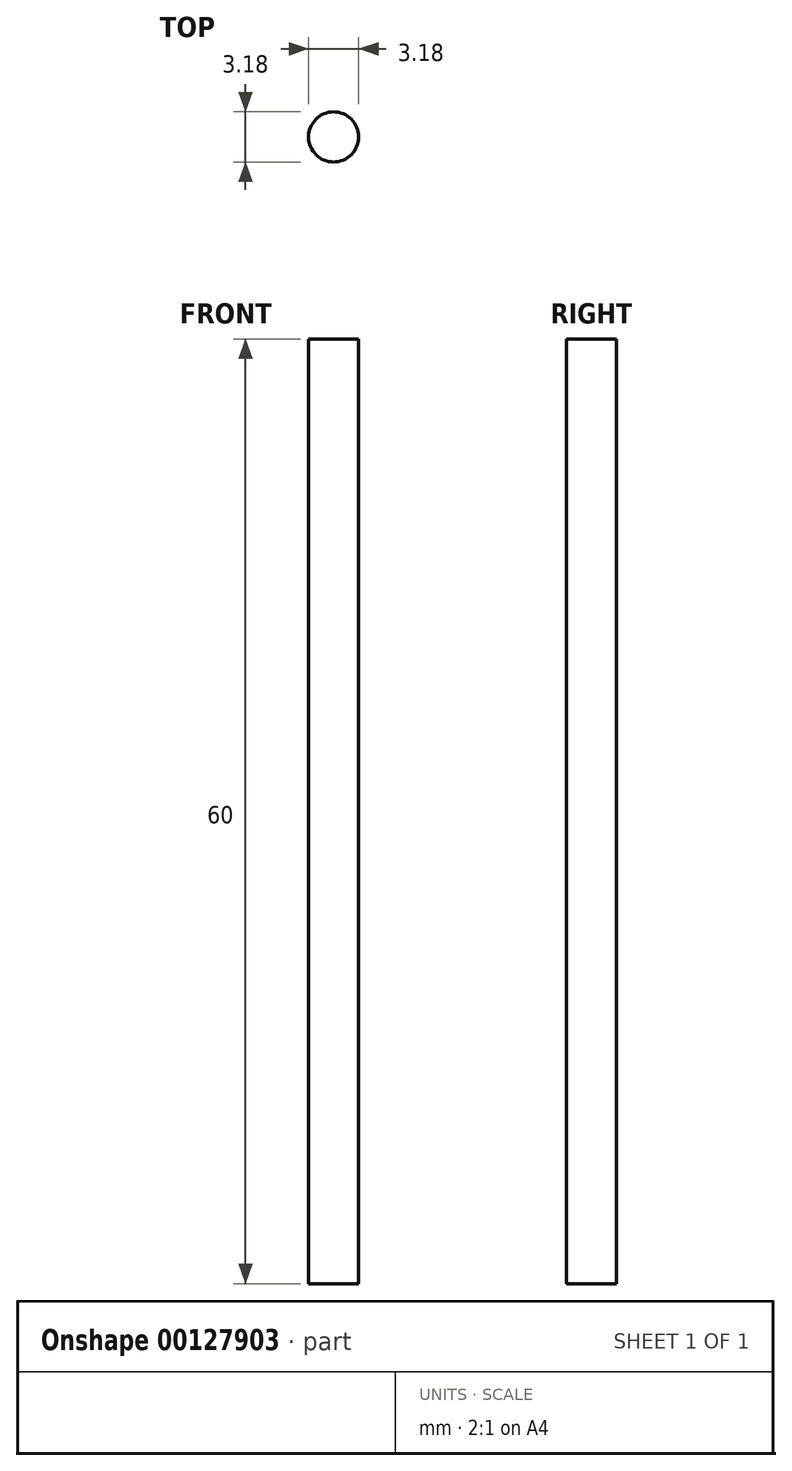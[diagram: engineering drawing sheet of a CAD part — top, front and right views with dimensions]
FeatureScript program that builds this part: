
annotation { "Feature Type Name" : "Feature", "Feature Type Description" : "" }
export const myFeature = defineFeature(function(context is Context, id is Id, definition is map)
    precondition{}
    {
        {
            var Q0;
            Q0=qCreatedBy(makeId("Top.planeOp"),FACE);
            var sketch = newSketch(context, id + "F0", { "sketchPlane" : qUnion([Q0])});
            skCircle(sketch, "E0", {"center": v(0, 0) * mm, "radius": 1.6 * mm});
            skSolve(sketch);
        }
        {
            var Q0;
            Q0 = qSketchRegion(id + "F0", true);
            extrude(context, id + "F1", {"entities" : qUnion([Q0]), "depth" : 60 * mm});
        }
    });
